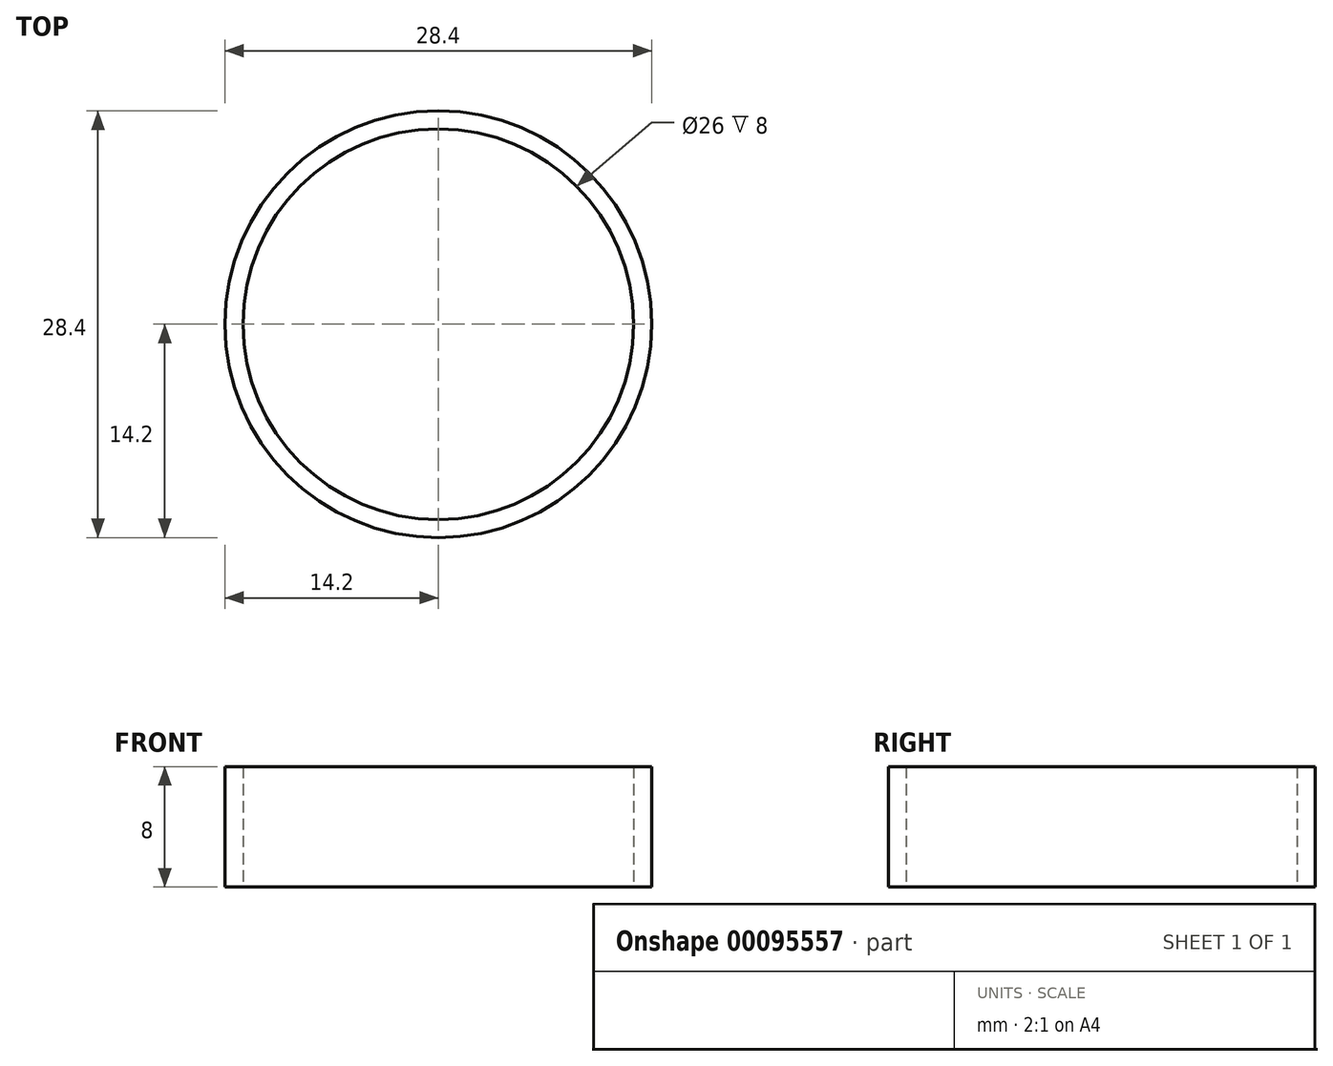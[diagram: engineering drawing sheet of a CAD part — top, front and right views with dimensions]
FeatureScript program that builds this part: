
annotation { "Feature Type Name" : "Feature", "Feature Type Description" : "" }
export const myFeature = defineFeature(function(context is Context, id is Id, definition is map)
    precondition{}
    {
        {
            var Q0;
            Q0=qCreatedBy(makeId("Top.planeOp"),FACE);
            var sketch = newSketch(context, id + "F0", { "sketchPlane" : qUnion([Q0])});
            skCircle(sketch, "E0", {"center": v(0, 0) * mm, "radius": 13 * mm});
            skCircle(sketch, "E1.0", {"center": v(0, 0) * mm, "radius": 14.2 * mm});
            skSolve(sketch);
        }
        {
            var Q0;
            Q0=makeQuery(id+"F0.imprint","IMPRINT",FACE,{"disambiguationData":[TD([[makeQuery(id+"F0.imprint","IMPRINT",EDGE,{"derivedFrom":sQuery(id+"F0.wireOp",EDGE,"E0")}),-1.0]])]});
            extrude(context, id + "F1", {"entities" : qUnion([Q0]), "depth" : 8 * mm});
        }
    });
